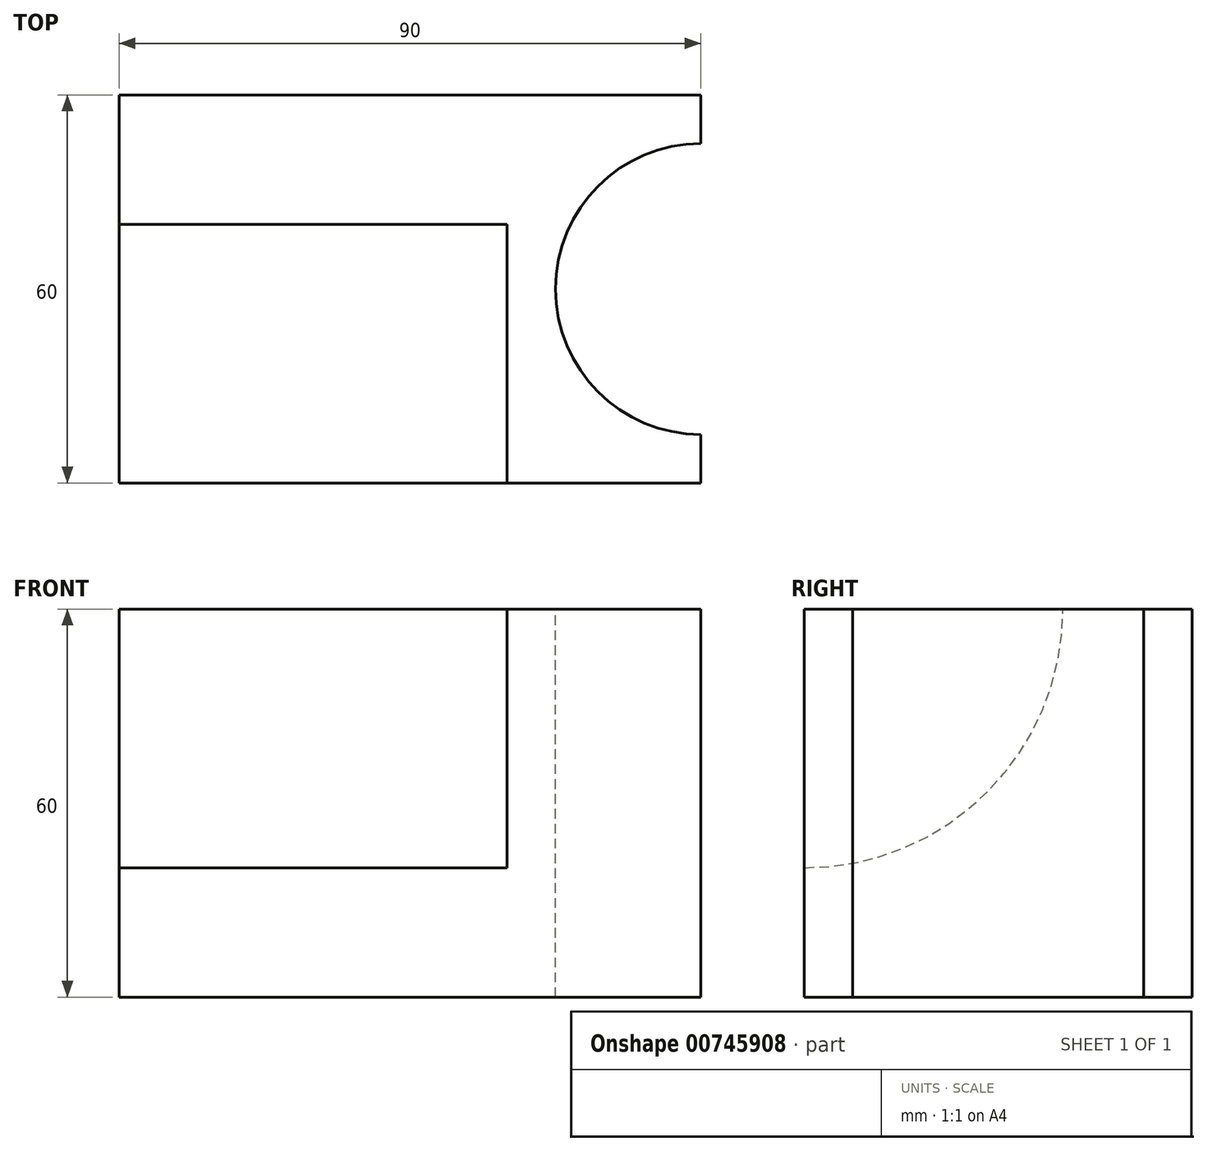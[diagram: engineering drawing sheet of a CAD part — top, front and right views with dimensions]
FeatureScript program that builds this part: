
annotation { "Feature Type Name" : "Feature", "Feature Type Description" : "" }
export const myFeature = defineFeature(function(context is Context, id is Id, definition is map)
    precondition{}
    {
        {
            var Q0;
            Q0=qCreatedBy(makeId("Front.planeOp"),FACE);
            var sketch = newSketch(context, id + "F0", { "sketchPlane" : qUnion([Q0])});
            skLineSegment(sketch, "E0.bottom", {"start": v(0, 0) * mm, "end": v(90, 0) * mm});
            skLineSegment(sketch, "E0.top", {"start": v(0, 60) * mm, "end": v(90, 60) * mm});
            skLineSegment(sketch, "E0.left", {"start": v(0, 0) * mm, "end": v(0, 60) * mm});
            skLineSegment(sketch, "E0.right", {"start": v(90, 0) * mm, "end": v(90, 60) * mm});
            skSolve(sketch);
        }
        {
            var Q0;
            Q0 = qSketchRegion(id + "F0", true);
            extrude(context, id + "F1", {"entities" : qUnion([Q0]), "depth" : 60 * mm, "offsetDistance" : 25 * mm});
        }
        {
            var Q0;
            Q0=makeQuery(id+"F1.opExtrude","SWEPT_FACE",FACE,{"disambiguationData":[OSD([sQuery(id+"F0.wireOp",EDGE,"E0.top")])]});
            var sketch = newSketch(context, id + "F2", { "sketchPlane" : qUnion([Q0])});
            skArc(sketch, "E1", {"start": v(94.63, -7.98) * mm, "mid": v(67.62, -27.67) * mm, "end": v(90, -52.5) * mm});
            skSolve(sketch);
        }
        {
            var Q0;
            {var subQ0=sQuery(id+"F2.wireOp",EDGE,"E1");var subQ1=makeQuery(id+"F1.opExtrude","SWEPT_EDGE",EDGE,{"disambiguationData":[OSD([sQuery(id+"F0.wireOp",EDGE,"E0.top"),sQuery(id+"F0.wireOp",EDGE,"E0.right")])]});var subQ2=makeQuery(id+"F2.imprint","INTERSECT",VERTEX,{"disambiguationData":[OD(0.0)],"derivedFrom":[subQ1,subQ0]});Q0=makeQuery(id+"F2.imprint","IMPRINT",FACE,{"disambiguationData":[TD([[makeQuery(id+"F2.imprint","IMPRINT",EDGE,{"disambiguationData":[TD([[subQ2,1.0]])],"derivedFrom":subQ0}),1.0]])]});}
            extrude(context, id + "F3", {"entities" : qUnion([Q0]), "operationType" : NewBodyOperationType.REMOVE, "endBound" : BoundingType.THROUGH_ALL, "oppositeDirection" : true, "depth" : 25 * mm, "offsetDistance" : 25 * mm});
        }
        {
            var Q0;
            Q0=makeQuery(id+"F1.opExtrude","SWEPT_FACE",FACE,{"disambiguationData":[OSD([sQuery(id+"F0.wireOp",EDGE,"E0.left")])]});
            var sketch = newSketch(context, id + "F4", { "sketchPlane" : qUnion([Q0])});
            skArc(sketch, "E2", {"start": v(20, 60) * mm, "mid": v(31.72, 31.72) * mm, "end": v(60, 20) * mm});
            skSolve(sketch);
        }
        {
            var Q0;
            {var subQ0=sQuery(id+"F4.wireOp",EDGE,"E2");var subQ1=sQuery(id+"F0.wireOp",EDGE,"E0.left");var subQ4=makeQuery(id+"F1.opExtrude","CAP_EDGE",EDGE,{"disambiguationData":[OSD([subQ1])],"isStart":false});var subQ5=makeQuery(id+"F4.imprint","INTERSECT",VERTEX,{"derivedFrom":[subQ4,subQ0]});Q0=makeQuery(id+"F4.imprint","IMPRINT",FACE,{"disambiguationData":[TD([[makeQuery(id+"F4.imprint","IMPRINT",EDGE,{"disambiguationData":[TD([[subQ5,1.0]])],"derivedFrom":subQ0}),1.0]])]});}
            extrude(context, id + "F5", {"entities" : qUnion([Q0]), "operationType" : NewBodyOperationType.REMOVE, "oppositeDirection" : true, "depth" : 60 * mm, "offsetDistance" : 25 * mm});
        }
    });
